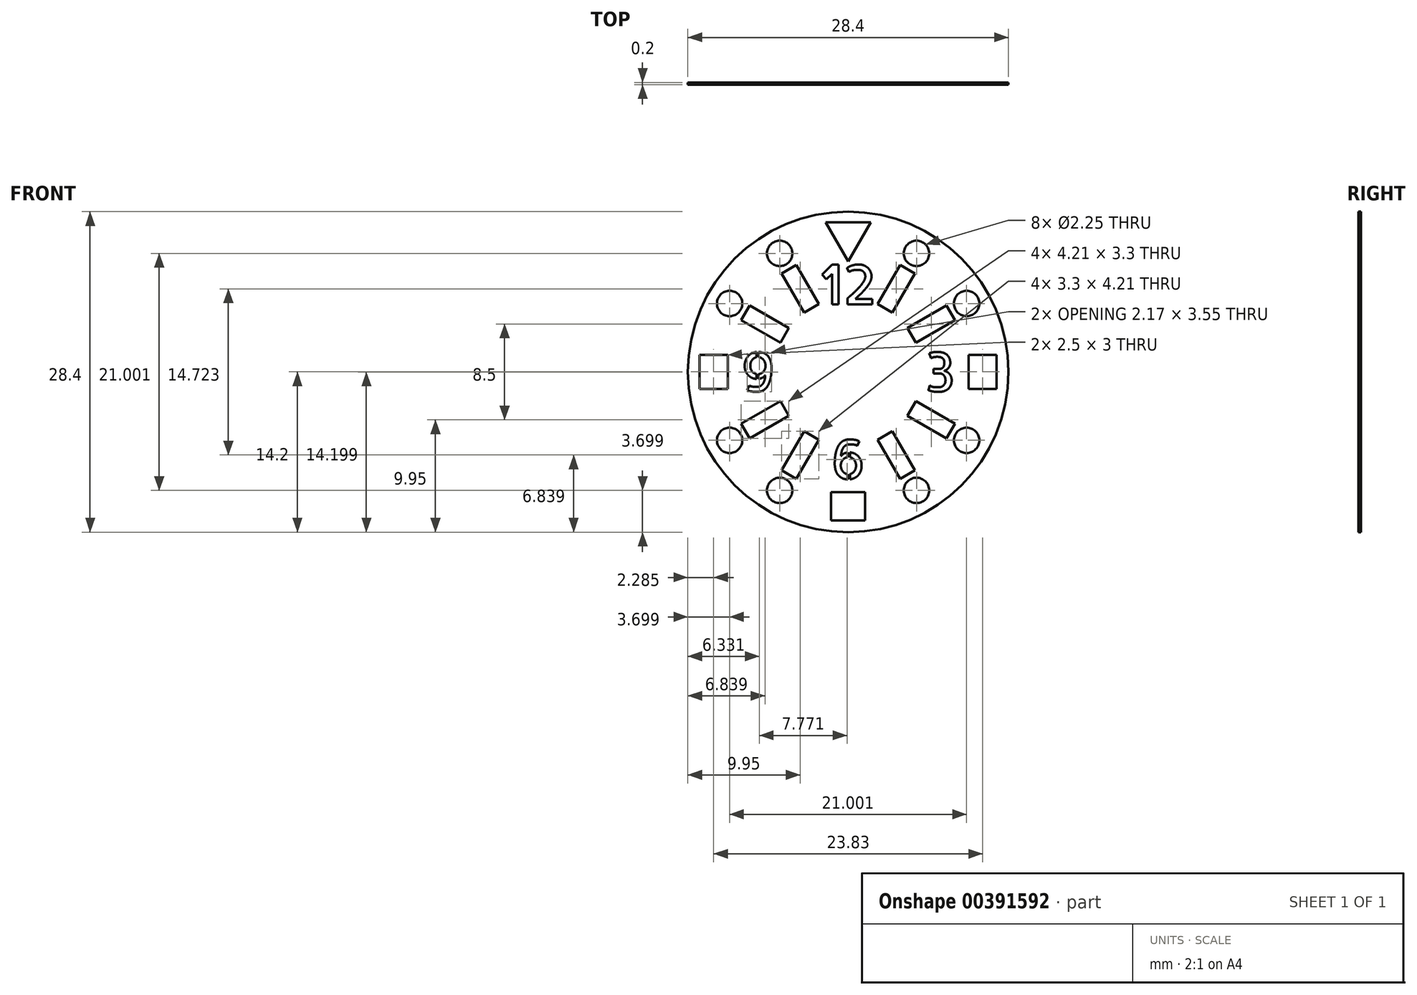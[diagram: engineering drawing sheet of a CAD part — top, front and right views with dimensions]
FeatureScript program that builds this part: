
annotation { "Feature Type Name" : "Feature", "Feature Type Description" : "" }
export const myFeature = defineFeature(function(context is Context, id is Id, definition is map)
    precondition{}
    {
        {
            var Q0;
            Q0=qCreatedBy(makeId("Front.planeOp"),FACE);
            var sketch = newSketch(context, id + "F0", { "sketchPlane" : qUnion([Q0])});
            skCircle(sketch, "E0", {"center": v(0, 0) * mm, "radius": 6.5 * mm, "construction": true});
            skCircle(sketch, "E1", {"center": v(0, 0) * mm, "radius": 10.5 * mm, "construction": true});
            skLineSegment(sketch, "E2", {"start": v(0, 6.5) * mm, "end": v(0.75, 6.5) * mm, "construction": true});
            skLineSegment(sketch, "E3", {"start": v(0.75, 6.5) * mm, "end": v(0.75, 10.5) * mm, "construction": true});
            skLineSegment(sketch, "E4", {"start": v(0.75, 10.5) * mm, "end": v(0, 10.5) * mm, "construction": true});
            skLineSegment(sketch, "E5", {"start": v(0, 10.5) * mm, "end": v(-0.75, 10.5) * mm, "construction": true});
            skLineSegment(sketch, "E6", {"start": v(-0.75, 10.5) * mm, "end": v(-0.75, 6.5) * mm, "construction": true});
            skLineSegment(sketch, "E7", {"start": v(-0.75, 6.5) * mm, "end": v(0, 6.5) * mm, "construction": true});
            skLineSegment(sketch, "E8.1.0", {"start": v(-2.6, 6) * mm, "end": v(-4.6, 9.47) * mm});
            skLineSegment(sketch, "E8.1.1", {"start": v(-5.9, 8.72) * mm, "end": v(-3.9, 5.25) * mm});
            skLineSegment(sketch, "E8.1.2", {"start": v(-3.9, 5.25) * mm, "end": v(-3.25, 5.63) * mm});
            skLineSegment(sketch, "E8.1.3", {"start": v(-3.25, 5.63) * mm, "end": v(-2.6, 6) * mm});
            skLineSegment(sketch, "E8.1.4", {"start": v(-4.6, 9.47) * mm, "end": v(-5.25, 9.1) * mm});
            skLineSegment(sketch, "E8.1.5", {"start": v(-5.25, 9.1) * mm, "end": v(-5.9, 8.72) * mm});
            skLineSegment(sketch, "E8.2.0", {"start": v(-5.25, 3.9) * mm, "end": v(-8.72, 5.9) * mm});
            skLineSegment(sketch, "E8.2.1", {"start": v(-9.47, 4.6) * mm, "end": v(-6, 2.6) * mm});
            skLineSegment(sketch, "E8.2.2", {"start": v(-6, 2.6) * mm, "end": v(-5.63, 3.25) * mm});
            skLineSegment(sketch, "E8.2.3", {"start": v(-5.63, 3.25) * mm, "end": v(-5.25, 3.9) * mm});
            skLineSegment(sketch, "E8.2.4", {"start": v(-8.72, 5.9) * mm, "end": v(-9.1, 5.25) * mm});
            skLineSegment(sketch, "E8.2.5", {"start": v(-9.1, 5.25) * mm, "end": v(-9.47, 4.6) * mm});
            skLineSegment(sketch, "E8.3.0", {"start": v(-6.5, 0.75) * mm, "end": v(-10.5, 0.75) * mm, "construction": true});
            skLineSegment(sketch, "E8.3.1", {"start": v(-10.5, -0.75) * mm, "end": v(-6.5, -0.75) * mm, "construction": true});
            skLineSegment(sketch, "E8.3.2", {"start": v(-6.5, -0.75) * mm, "end": v(-6.5, 0) * mm, "construction": true});
            skLineSegment(sketch, "E8.3.3", {"start": v(-6.5, 0) * mm, "end": v(-6.5, 0.75) * mm, "construction": true});
            skLineSegment(sketch, "E8.3.4", {"start": v(-10.5, 0.75) * mm, "end": v(-10.5, 0) * mm, "construction": true});
            skLineSegment(sketch, "E8.3.5", {"start": v(-10.5, 0) * mm, "end": v(-10.5, -0.75) * mm, "construction": true});
            skLineSegment(sketch, "E8.4.0", {"start": v(-6, -2.6) * mm, "end": v(-9.47, -4.6) * mm});
            skLineSegment(sketch, "E8.4.1", {"start": v(-8.72, -5.9) * mm, "end": v(-5.25, -3.9) * mm});
            skLineSegment(sketch, "E8.4.2", {"start": v(-5.25, -3.9) * mm, "end": v(-5.63, -3.25) * mm});
            skLineSegment(sketch, "E8.4.3", {"start": v(-5.63, -3.25) * mm, "end": v(-6, -2.6) * mm});
            skLineSegment(sketch, "E8.4.4", {"start": v(-9.47, -4.6) * mm, "end": v(-9.1, -5.25) * mm});
            skLineSegment(sketch, "E8.4.5", {"start": v(-9.1, -5.25) * mm, "end": v(-8.72, -5.9) * mm});
            skLineSegment(sketch, "E8.5.0", {"start": v(-3.9, -5.25) * mm, "end": v(-5.9, -8.72) * mm});
            skLineSegment(sketch, "E8.5.1", {"start": v(-4.6, -9.47) * mm, "end": v(-2.6, -6) * mm});
            skLineSegment(sketch, "E8.5.2", {"start": v(-2.6, -6) * mm, "end": v(-3.25, -5.63) * mm});
            skLineSegment(sketch, "E8.5.3", {"start": v(-3.25, -5.63) * mm, "end": v(-3.9, -5.25) * mm});
            skLineSegment(sketch, "E8.5.4", {"start": v(-5.9, -8.72) * mm, "end": v(-5.25, -9.1) * mm});
            skLineSegment(sketch, "E8.5.5", {"start": v(-5.25, -9.1) * mm, "end": v(-4.6, -9.47) * mm});
            skLineSegment(sketch, "E8.6.0", {"start": v(-0.75, -6.5) * mm, "end": v(-0.75, -10.5) * mm, "construction": true});
            skLineSegment(sketch, "E8.6.1", {"start": v(0.75, -10.5) * mm, "end": v(0.75, -6.5) * mm, "construction": true});
            skLineSegment(sketch, "E8.6.2", {"start": v(0.75, -6.5) * mm, "end": v(0, -6.5) * mm, "construction": true});
            skLineSegment(sketch, "E8.6.3", {"start": v(0, -6.5) * mm, "end": v(-0.75, -6.5) * mm, "construction": true});
            skLineSegment(sketch, "E8.6.4", {"start": v(-0.75, -10.5) * mm, "end": v(0, -10.5) * mm, "construction": true});
            skLineSegment(sketch, "E8.6.5", {"start": v(0, -10.5) * mm, "end": v(0.75, -10.5) * mm, "construction": true});
            skLineSegment(sketch, "E8.7.0", {"start": v(2.6, -6) * mm, "end": v(4.6, -9.47) * mm});
            skLineSegment(sketch, "E8.7.1", {"start": v(5.9, -8.72) * mm, "end": v(3.9, -5.25) * mm});
            skLineSegment(sketch, "E8.7.2", {"start": v(3.9, -5.25) * mm, "end": v(3.25, -5.63) * mm});
            skLineSegment(sketch, "E8.7.3", {"start": v(3.25, -5.63) * mm, "end": v(2.6, -6) * mm});
            skLineSegment(sketch, "E8.7.4", {"start": v(4.6, -9.47) * mm, "end": v(5.25, -9.1) * mm});
            skLineSegment(sketch, "E8.7.5", {"start": v(5.25, -9.1) * mm, "end": v(5.9, -8.72) * mm});
            skLineSegment(sketch, "E8.8.0", {"start": v(5.25, -3.9) * mm, "end": v(8.72, -5.9) * mm});
            skLineSegment(sketch, "E8.8.1", {"start": v(9.47, -4.6) * mm, "end": v(6, -2.6) * mm});
            skLineSegment(sketch, "E8.8.2", {"start": v(6, -2.6) * mm, "end": v(5.63, -3.25) * mm});
            skLineSegment(sketch, "E8.8.3", {"start": v(5.63, -3.25) * mm, "end": v(5.25, -3.9) * mm});
            skLineSegment(sketch, "E8.8.4", {"start": v(8.72, -5.9) * mm, "end": v(9.1, -5.25) * mm});
            skLineSegment(sketch, "E8.8.5", {"start": v(9.1, -5.25) * mm, "end": v(9.47, -4.6) * mm});
            skLineSegment(sketch, "E8.9.0", {"start": v(6.5, -0.75) * mm, "end": v(10.5, -0.75) * mm, "construction": true});
            skLineSegment(sketch, "E8.9.1", {"start": v(10.5, 0.75) * mm, "end": v(6.5, 0.75) * mm, "construction": true});
            skLineSegment(sketch, "E8.9.2", {"start": v(6.5, 0.75) * mm, "end": v(6.5, 0) * mm, "construction": true});
            skLineSegment(sketch, "E8.9.3", {"start": v(6.5, 0) * mm, "end": v(6.5, -0.75) * mm, "construction": true});
            skLineSegment(sketch, "E8.9.4", {"start": v(10.5, -0.75) * mm, "end": v(10.5, 0) * mm, "construction": true});
            skLineSegment(sketch, "E8.9.5", {"start": v(10.5, 0) * mm, "end": v(10.5, 0.75) * mm, "construction": true});
            skLineSegment(sketch, "E8.10.0", {"start": v(6, 2.6) * mm, "end": v(9.47, 4.6) * mm});
            skLineSegment(sketch, "E8.10.1", {"start": v(8.72, 5.9) * mm, "end": v(5.25, 3.9) * mm});
            skLineSegment(sketch, "E8.10.2", {"start": v(5.25, 3.9) * mm, "end": v(5.63, 3.25) * mm});
            skLineSegment(sketch, "E8.10.3", {"start": v(5.63, 3.25) * mm, "end": v(6, 2.6) * mm});
            skLineSegment(sketch, "E8.10.4", {"start": v(9.47, 4.6) * mm, "end": v(9.1, 5.25) * mm});
            skLineSegment(sketch, "E8.10.5", {"start": v(9.1, 5.25) * mm, "end": v(8.72, 5.9) * mm});
            skLineSegment(sketch, "E8.11.0", {"start": v(3.9, 5.25) * mm, "end": v(5.9, 8.72) * mm});
            skLineSegment(sketch, "E8.11.1", {"start": v(4.6, 9.47) * mm, "end": v(2.6, 6) * mm});
            skLineSegment(sketch, "E8.11.2", {"start": v(2.6, 6) * mm, "end": v(3.25, 5.63) * mm});
            skLineSegment(sketch, "E8.11.3", {"start": v(3.25, 5.63) * mm, "end": v(3.9, 5.25) * mm});
            skLineSegment(sketch, "E8.11.4", {"start": v(5.9, 8.72) * mm, "end": v(5.25, 9.1) * mm});
            skLineSegment(sketch, "E8.11.5", {"start": v(5.25, 9.1) * mm, "end": v(4.6, 9.47) * mm});
            skSolve(sketch);
        }
        {
            var Q0;
            Q0=qCreatedBy(makeId("Front.planeOp"),FACE);
            var sketch = newSketch(context, id + "F1", { "sketchPlane" : qUnion([Q0])});
            skText(sketch, "E9", { "text": "12", "fontName": "AllertaStencil-Regular.ttf"});
            skText(sketch, "E10", { "text": "6", "fontName": "AllertaStencil-Regular.ttf"});
            skText(sketch, "E11", { "text": "9", "fontName": "AllertaStencil-Regular.ttf"});
            skPoint(sketch, "E12", {"position": v(-9.5, 0) * mm});
            skText(sketch, "E13", { "text": "3", "fontName": "AllertaStencil-Regular.ttf"});
            skPoint(sketch, "E14", {"position": v(9.5, 0) * mm});
            skCircle(sketch, "E15", {"center": v(0, 0) * mm, "radius": 6 * mm, "construction": true});
            skCircle(sketch, "E16", {"center": v(0, 0) * mm, "radius": 9.5 * mm, "construction": true});
            const initialGuessF1  = {"E9": [-0.00246, 0.006, 1, 0, 0.0035], "E10": [-0.00153, -0.0095, 1, 0, 0.0035], "E11": [-0.0095, -0.00175, 1, 0, 0.0035], "E13": [0.00676, -0.00175, 1, 0, 0.0035]};
            skSetInitialGuess(sketch, initialGuessF1);
            skSolve(sketch);
        }
        {
            var Q0;
            Q0=qCreatedBy(makeId("Front.planeOp"),FACE);
            var sketch = newSketch(context, id + "F2", { "sketchPlane" : qUnion([Q0])});
            skLineSegment(sketch, "E17", {"start": v(0, 9.79) * mm, "end": v(2, 13.25) * mm});
            skLineSegment(sketch, "E18", {"start": v(2, 13.25) * mm, "end": v(-2, 13.25) * mm});
            skLineSegment(sketch, "E19", {"start": v(-2, 13.25) * mm, "end": v(0, 9.79) * mm});
            skLineSegment(sketch, "E20", {"start": v(-10.66, 0) * mm, "end": v(-10.66, 1.5) * mm});
            skLineSegment(sketch, "E21", {"start": v(-10.66, 1.5) * mm, "end": v(-13.16, 1.5) * mm});
            skLineSegment(sketch, "E22", {"start": v(-13.16, 1.5) * mm, "end": v(-13.16, -1.5) * mm});
            skLineSegment(sketch, "E23", {"start": v(-13.16, -1.5) * mm, "end": v(-10.66, -1.5) * mm});
            skLineSegment(sketch, "E24", {"start": v(-10.66, -1.5) * mm, "end": v(-10.66, 0) * mm});
            skCircle(sketch, "E25", {"center": v(0, 0) * mm, "radius": 11 * mm, "construction": true});
            skLineSegment(sketch, "E26.1.0", {"start": v(-1.5, -10.66) * mm, "end": v(-1.5, -13.16) * mm});
            skLineSegment(sketch, "E26.1.1", {"start": v(-1.5, -13.16) * mm, "end": v(1.5, -13.16) * mm});
            skLineSegment(sketch, "E26.1.2", {"start": v(1.5, -13.16) * mm, "end": v(1.5, -10.66) * mm});
            skLineSegment(sketch, "E26.1.3", {"start": v(1.5, -10.66) * mm, "end": v(0, -10.66) * mm});
            skLineSegment(sketch, "E26.1.4", {"start": v(0, -10.66) * mm, "end": v(-1.5, -10.66) * mm});
            skLineSegment(sketch, "E26.2.0", {"start": v(10.66, -1.5) * mm, "end": v(13.16, -1.5) * mm});
            skLineSegment(sketch, "E26.2.1", {"start": v(13.16, -1.5) * mm, "end": v(13.16, 1.5) * mm});
            skLineSegment(sketch, "E26.2.2", {"start": v(13.16, 1.5) * mm, "end": v(10.66, 1.5) * mm});
            skLineSegment(sketch, "E26.2.3", {"start": v(10.66, 1.5) * mm, "end": v(10.66, 0) * mm});
            skLineSegment(sketch, "E26.2.4", {"start": v(10.66, 0) * mm, "end": v(10.66, -1.5) * mm});
            skLineSegment(sketch, "E26.anchor1", {"start": v(0, 0) * mm, "end": v(-10.66, 0) * mm, "construction": true});
            skLineSegment(sketch, "E26.anchor2", {"start": v(0, 0) * mm, "end": v(10.66, 0) * mm, "construction": true});
            skCircle(sketch, "E27", {"center": v(0, 0) * mm, "radius": 14.2 * mm, "construction": true});
            skCircle(sketch, "E28", {"center": v(0, 0) * mm, "radius": 13.25 * mm, "construction": true});
            skLineSegment(sketch, "E29", {"start": v(0, 13.25) * mm, "end": v(0, 11) * mm, "construction": true});
            skCircle(sketch, "E30", {"center": v(0, 12.12) * mm, "radius": 1.13 * mm, "construction": true});
            skCircle(sketch, "E31.1.0", {"center": v(-6.06, 10.5) * mm, "radius": 1.13 * mm});
            skCircle(sketch, "E31.2.0", {"center": v(-10.5, 6.06) * mm, "radius": 1.13 * mm});
            skCircle(sketch, "E31.3.0", {"center": v(-12.12, 0) * mm, "radius": 1.13 * mm, "construction": true});
            skCircle(sketch, "E31.4.0", {"center": v(-10.5, -6.06) * mm, "radius": 1.13 * mm});
            skCircle(sketch, "E31.5.0", {"center": v(-6.06, -10.5) * mm, "radius": 1.13 * mm});
            skCircle(sketch, "E31.6.0", {"center": v(0, -12.12) * mm, "radius": 1.13 * mm, "construction": true});
            skCircle(sketch, "E31.7.0", {"center": v(6.06, -10.5) * mm, "radius": 1.13 * mm});
            skCircle(sketch, "E31.8.0", {"center": v(10.5, -6.06) * mm, "radius": 1.13 * mm});
            skCircle(sketch, "E31.9.0", {"center": v(12.12, 0) * mm, "radius": 1.13 * mm, "construction": true});
            skCircle(sketch, "E31.10.0", {"center": v(10.5, 6.06) * mm, "radius": 1.13 * mm});
            skCircle(sketch, "E31.11.0", {"center": v(6.06, 10.5) * mm, "radius": 1.13 * mm});
            skSolve(sketch);
        }
        {
            var Q0;
            Q0=qCreatedBy(makeId("Front.planeOp"),FACE);
            var sketch = newSketch(context, id + "F3", { "sketchPlane" : qUnion([Q0])});
            skCircle(sketch, "E32", {"center": v(0, 0) * mm, "radius": 14.2 * mm});
            skSolve(sketch);
        }
        {
            var Q0;
            Q0 = qSketchRegion(id + "F3", true);
            extrude(context, id + "F4", {"entities" : qUnion([Q0]), "depth" : 0.2 * mm});
        }
        {
            var Q0;
            Q0 = qSketchRegion(id + "F2", true);
            var Q1;
            Q1 = qSketchRegion(id + "F1", true);
            var Q2;
            Q2 = qSketchRegion(id + "F0", true);
            extrude(context, id + "F5", {"entities" : qUnion([Q0, Q1, Q2]), "operationType" : NewBodyOperationType.REMOVE, "depth" : 25 * mm});
        }
    });
